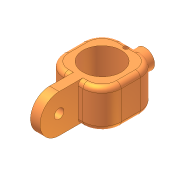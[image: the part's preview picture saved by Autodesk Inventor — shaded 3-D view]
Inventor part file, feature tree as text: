
AUTODESK INVENTOR PART (.ipt)
format: ipt  version: unknown  size: 301,568 bytes
history: native  units: mm
features: extrude x4, sketch x4, fillet x3
ambient origin geometry x8: Origin, YZ Plane, XZ Plane, XY Plane, X Axis, Y Axis, Z Axis, Center Point
feature tree (11):
  extrude  "Extrusion1"  Depth=4.0mm TaperAngle=0.0deg
  extrude  "Extrusion3"  Depth=1.0mm
  fillet  "Fillet2"  Radius=4.0mm
  fillet  "Fillet3"  Radius=2.0mm
  extrude  "Extrusion4"  Depth=2.0mm
  extrude  "Extrusion5"  Depth=1.0mm
  fillet  "Fillet4"  Radius=3.0mm
  sketch  "Sketch1"  dims[d0=4.0mm d7=4.0mm d8=0.0mm]
  sketch  "Sketch3"  dims[d13=3.0mm d14=1.0mm d15=4.0mm d16=2.0mm]
  sketch  "Sketch4"  dims[d17=1.5mm d18=0.0mm d19=2.0mm]
  sketch  "Sketch5"  dims[d20=2.0mm d21=1.0mm d22=3.0mm d23=0.0mm d24=0.5mm d25=10.0mm d26=0.0mm d27=0.5mm]
